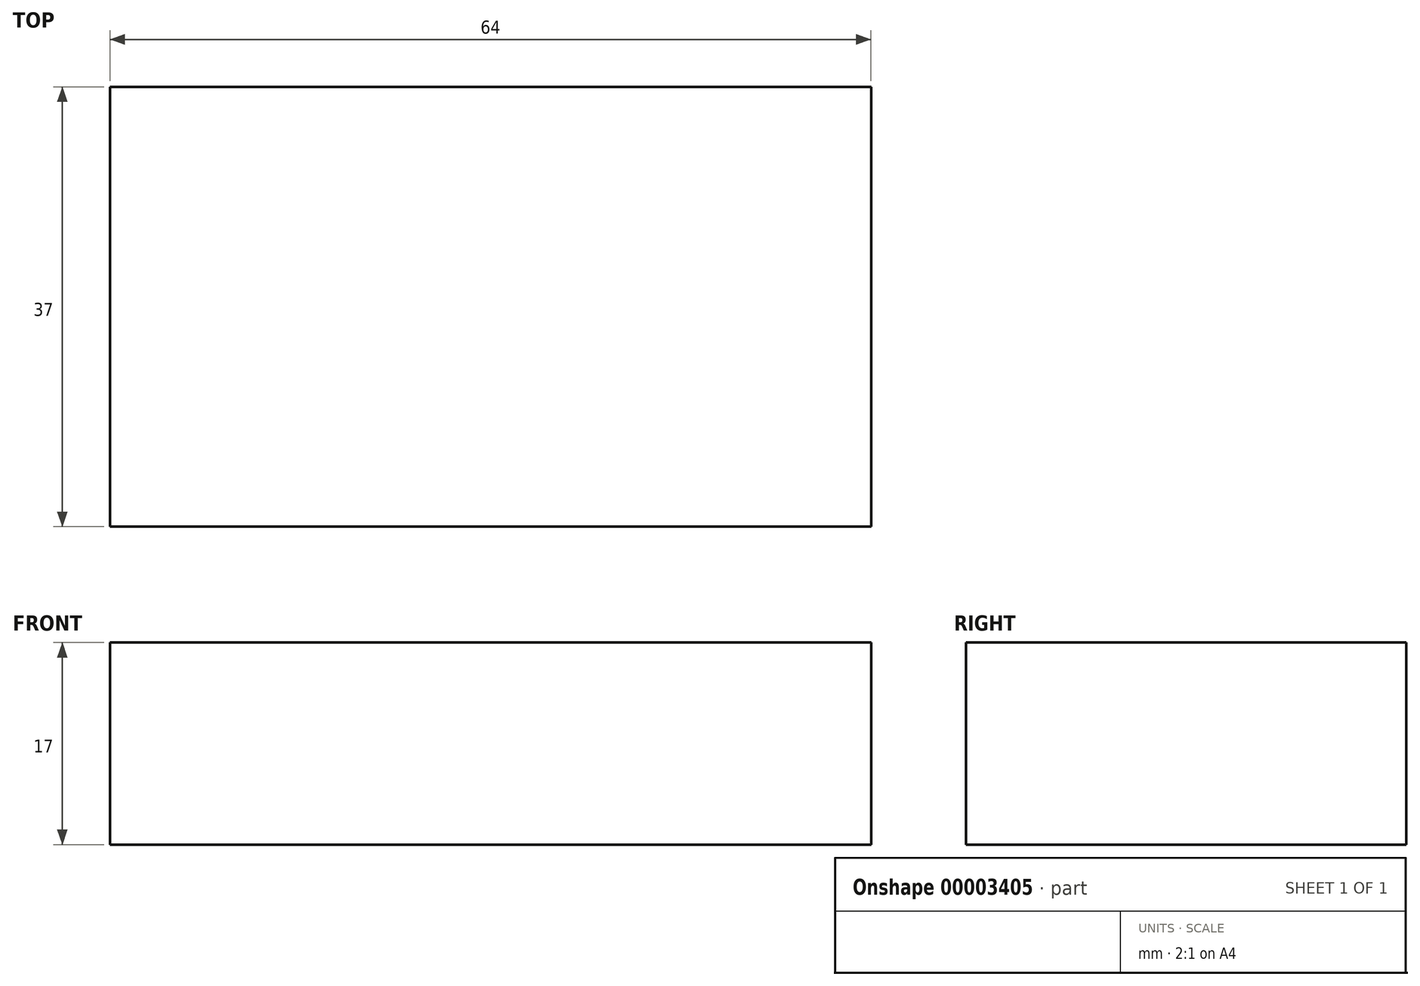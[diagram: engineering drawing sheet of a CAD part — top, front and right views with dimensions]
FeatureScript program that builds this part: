
annotation { "Feature Type Name" : "Feature", "Feature Type Description" : "" }
export const myFeature = defineFeature(function(context is Context, id is Id, definition is map)
    precondition{}
    {
        {
            var Q0;
            Q0=qCreatedBy(makeId("Top.planeOp"),FACE);
            var sketch = newSketch(context, id + "F0", { "sketchPlane" : qUnion([Q0])});
            skLineSegment(sketch, "E0.bottom", {"start": v(-67.3, -7.64) * mm, "end": v(-3.3, -7.64) * mm});
            skLineSegment(sketch, "E0.top", {"start": v(-67.3, -44.64) * mm, "end": v(-3.3, -44.64) * mm});
            skLineSegment(sketch, "E0.left", {"start": v(-67.3, -7.64) * mm, "end": v(-67.3, -44.64) * mm});
            skLineSegment(sketch, "E0.right", {"start": v(-3.3, -7.64) * mm, "end": v(-3.3, -44.64) * mm});
            skSolve(sketch);
        }
        {
            var Q0;
            Q0=makeQuery(id+"F0.imprint","IMPRINT",FACE,{"disambiguationData":[TD([[makeQuery(id+"F0.imprint","IMPRINT",EDGE,{"derivedFrom":sQuery(id+"F0.wireOp",EDGE,"E0.bottom")}),-1.0]])]});
            extrude(context, id + "F1", {"entities" : qUnion([Q0]), "depth" : 17 * mm});
        }
    });
